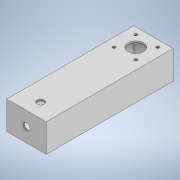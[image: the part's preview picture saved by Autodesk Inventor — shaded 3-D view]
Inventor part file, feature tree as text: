
AUTODESK INVENTOR PART (.ipt)
format: ipt  version: 2020 (Build 240168000, 168)  size: 147,968 bytes
history: native  units: mm
features: extrude x4, sketch x4, shell x1
ambient origin geometry x8: Origin, YZ Plane, XZ Plane, XY Plane, X Axis, Y Axis, Z Axis, Center Point
bodies: Body1 (feature_tree)
feature tree (9):
  extrude  "Extrusion1"  Depth=40.0mm
  shell  "Shell1"  Thickness=180.0mm
  extrude  "Extrusion2"  Depth=10.0mm
  extrude  "Extrusion3"  Depth=40.0mm
  extrude  "Extrusion4"  Depth=2.0mm
  sketch  "Sketch1"  dims[d1=56.0mm d2=40.0mm d3=180.0mm d4=0.0mm]
  sketch  "Sketch2"  dims[d5=2.0mm d6=10.0mm]
  sketch  "Sketch3"  dims[d7=180.0mm d8=0.0mm d9=40.0mm]
  sketch  "Sketch4"  dims[d10=4.0mm d11=22.0mm d12=115.0mm d13=31.0mm d14=2.0mm d15=0.0mm d16=10.0mm d17=10.0mm d18=2.0mm d19=0.0mm]
